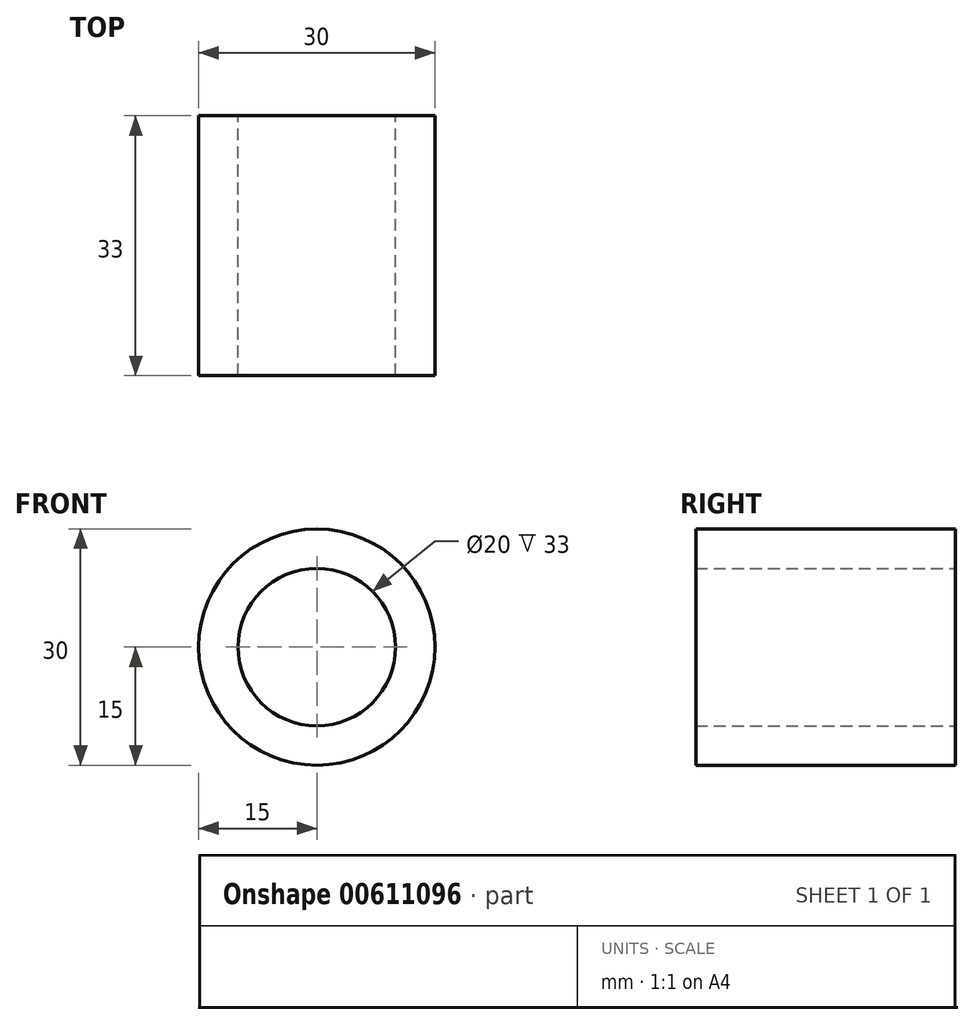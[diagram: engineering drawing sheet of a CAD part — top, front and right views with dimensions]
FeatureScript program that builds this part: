
annotation { "Feature Type Name" : "Feature", "Feature Type Description" : "" }
export const myFeature = defineFeature(function(context is Context, id is Id, definition is map)
    precondition{}
    {
        {
            var Q0;
            Q0=qCreatedBy(makeId("Front.planeOp"),FACE);
            var sketch = newSketch(context, id + "F0", { "sketchPlane" : qUnion([Q0])});
            skCircle(sketch, "E0", {"center": v(0, 0) * mm, "radius": 15 * mm});
            skCircle(sketch, "E1", {"center": v(0, 0) * mm, "radius": 10 * mm});
            skSolve(sketch);
        }
        {
            var Q0;
            Q0 = qSketchRegion(id + "F0", true);
            extrude(context, id + "F1", {"entities" : qUnion([Q0]), "depth" : 33 * mm, "offsetDistance" : 25 * mm});
        }
    });
